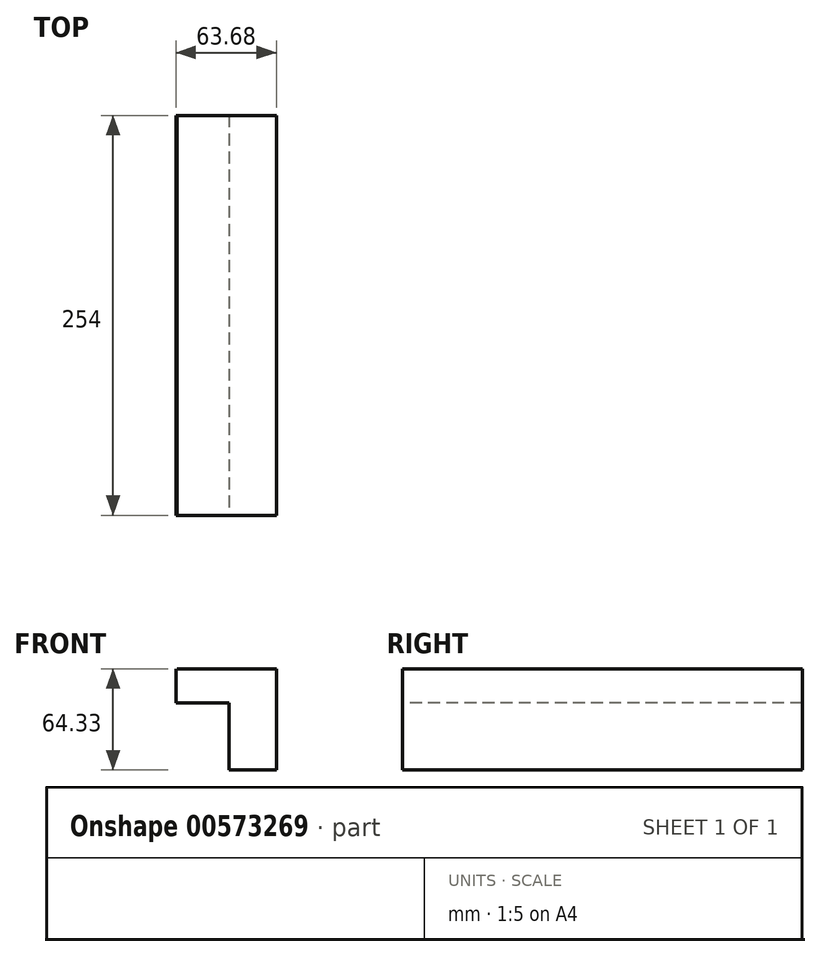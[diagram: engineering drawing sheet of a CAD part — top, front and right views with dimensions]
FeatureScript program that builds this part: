
annotation { "Feature Type Name" : "Feature", "Feature Type Description" : "" }
export const myFeature = defineFeature(function(context is Context, id is Id, definition is map)
    precondition{}
    {
        {
            var Q0;
            Q0=qCreatedBy(makeId("Front.planeOp"),FACE);
            var sketch = newSketch(context, id + "F0", { "sketchPlane" : qUnion([Q0])});
            skLineSegment(sketch, "E0", {"start": v(-63.03, 64.33) * mm, "end": v(0, 64.33) * mm});
            skLineSegment(sketch, "E1", {"start": v(0, 64.33) * mm, "end": v(0, 0) * mm});
            skLineSegment(sketch, "E2", {"start": v(0, 0) * mm, "end": v(-30.04, 0) * mm});
            skLineSegment(sketch, "E3", {"start": v(-30.04, 0) * mm, "end": v(-30.04, 42.78) * mm});
            skLineSegment(sketch, "E4", {"start": v(-63.68, 64.33) * mm, "end": v(-63.68, 42.78) * mm});
            skLineSegment(sketch, "E5", {"start": v(-63.68, 42.78) * mm, "end": v(-30.04, 42.78) * mm});
            skSolve(sketch);
        }
        {
            var Q0;
            Q0 = qSketchRegion(id + "F0", true);
            var Q1;
            Q1=sQuery(id+"F0.wireOp",EDGE,"E4");
            var Q2;
            Q2=sQuery(id+"F0.wireOp",EDGE,"E0");
            var Q3;
            Q3=sQuery(id+"F0.wireOp",EDGE,"E5");
            var Q4;
            Q4=sQuery(id+"F0.wireOp",EDGE,"E3");
            var Q5;
            Q5=sQuery(id+"F0.wireOp",EDGE,"E1");
            var Q6;
            Q6=sQuery(id+"F0.wireOp",EDGE,"E2");
            extrude(context, id + "F1", {"entities" : qUnion([Q0]), "bodyType" : ToolBodyType.SURFACE, "surfaceEntities" : qUnion([Q1, Q2, Q3, Q4, Q5, Q6]), "depth" : 254 * mm, "offsetDistance" : 25.4 * mm});
        }
    });
